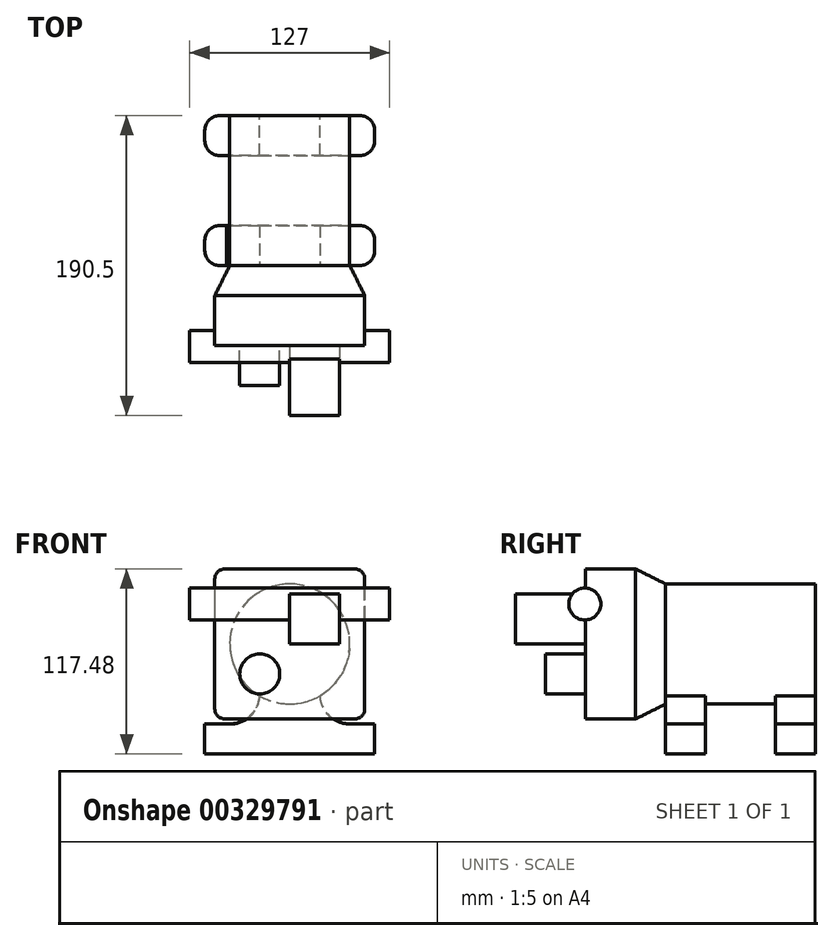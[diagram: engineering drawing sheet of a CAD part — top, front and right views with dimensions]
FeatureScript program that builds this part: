
annotation { "Feature Type Name" : "Feature", "Feature Type Description" : "" }
export const myFeature = defineFeature(function(context is Context, id is Id, definition is map)
    precondition{}
    {
        {
            var Q0;
            Q0=qCreatedBy(makeId("Front.planeOp"),FACE);
            var sketch = newSketch(context, id + "F0", { "sketchPlane" : qUnion([Q0])});
            skCircle(sketch, "E0", {"center": v(0, 0) * mm, "radius": 38.1 * mm});
            skSolve(sketch);
        }
        {
            var Q0;
            Q0 = qSketchRegion(id + "F0", true);
            extrude(context, id + "F1", {"entities" : qUnion([Q0]), "depth" : 95.25 * mm});
        }
        {
            var Q0;
            Q0=makeQuery(id+"F1.opExtrude","CAP_FACE",FACE,{"disambiguationData":[OSD([sQuery(id+"F0.wireOp",EDGE,"E0")])],"isStart":false});
            var sketch = newSketch(context, id + "F2", { "sketchPlane" : qUnion([Q0])});
            skLineSegment(sketch, "E1.bottom", {"start": v(47.63, -47.63) * mm, "end": v(-47.62, -47.63) * mm});
            skLineSegment(sketch, "E1.top", {"start": v(47.62, 47.63) * mm, "end": v(-47.63, 47.62) * mm});
            skLineSegment(sketch, "E1.left", {"start": v(47.63, -47.63) * mm, "end": v(47.62, 47.63) * mm});
            skLineSegment(sketch, "E1.right", {"start": v(-47.62, -47.63) * mm, "end": v(-47.63, 47.62) * mm});
            skPoint(sketch, "E1.middle", {"position": v(0, 0) * mm});
            skPoint(sketch, "E2.visualSharp", {"position": v(47.62, 47.63) * mm});
            skPoint(sketch, "E3.visualSharp", {"position": v(47.63, -47.63) * mm});
            skPoint(sketch, "E4.visualSharp", {"position": v(-47.62, -47.63) * mm});
            skPoint(sketch, "E5.visualSharp", {"position": v(-47.63, 47.62) * mm});
            skSolve(sketch);
        }
        {
            var Q0;
            Q0 = qSketchRegion(id + "F2", true);
            extrude(context, id + "F3", {"entities" : qUnion([Q0]), "depth" : 50.8 * mm, "hasSecondDirection" : true, "secondDirectionOppositeDirection" : false, "secondDirectionDepth" : 19.05 * mm});
        }
        {
            var Q0;
            Q0=makeQuery(id+"F3.opExtrude","SWEPT_EDGE",EDGE,{"disambiguationData":[OSD([sQuery(id+"F2.wireOp",EDGE,"E1.top"),sQuery(id+"F2.wireOp",EDGE,"E1.left")])]});
            var Q1;
            Q1=makeQuery(id+"F3.opExtrude","SWEPT_EDGE",EDGE,{"disambiguationData":[OSD([sQuery(id+"F2.wireOp",EDGE,"E1.bottom"),sQuery(id+"F2.wireOp",EDGE,"E1.left")])]});
            var Q2;
            Q2=makeQuery(id+"F3.opExtrude","SWEPT_EDGE",EDGE,{"disambiguationData":[OSD([sQuery(id+"F2.wireOp",EDGE,"E1.top"),sQuery(id+"F2.wireOp",EDGE,"E1.right")])]});
            var Q3;
            Q3=makeQuery(id+"F3.opExtrude","SWEPT_EDGE",EDGE,{"disambiguationData":[OSD([sQuery(id+"F2.wireOp",EDGE,"E1.bottom"),sQuery(id+"F2.wireOp",EDGE,"E1.right")])]});
            fillet(context, id + "F4", {"entities" : qUnion([Q0, Q1, Q2, Q3]), "radius" : 6.35 * mm, "tangentPropagation" : true, "allowEdgeOverflow" : false});
        }
        {
            var Q1;
            Q1=makeQuery(id+"F3.opExtrude","CAP_FACE",FACE,{"disambiguationData":[OSD([sQuery(id+"F2.wireOp",EDGE,"E1.bottom"),sQuery(id+"F2.wireOp",EDGE,"E1.top"),sQuery(id+"F2.wireOp",EDGE,"E1.left"),sQuery(id+"F2.wireOp",EDGE,"E1.right")])],"isStart":true});
            var Q2;
            Q2=makeQuery(id+"F1.opExtrude","CAP_FACE",FACE,{"disambiguationData":[OSD([sQuery(id+"F0.wireOp",EDGE,"E0")])],"isStart":false});
            loft(context, id + "F5", {"operationType" : NewBodyOperationType.ADD, "sheetProfilesArray" : [{ "sheetProfileEntities" : qUnion([Q1]) }, { "sheetProfileEntities" : qUnion([Q2]) }]});
        }
        {
            var Q0;
            Q0=qCreatedBy(makeId("Right.planeOp"),FACE);
            var sketch = newSketch(context, id + "F6", { "sketchPlane" : qUnion([Q0])});
            skCircle(sketch, "E6", {"center": v(-146.57, 25.4) * mm, "radius": 10.16 * mm});
            skSolve(sketch);
        }
        {
            var Q0;
            {var subQ0=sQuery(id+"F2.wireOp",EDGE,"E1.left");var subQ1=sQuery(id+"F2.wireOp",EDGE,"E1.bottom");var subQ2=sQuery(id+"F2.wireOp",EDGE,"E1.right");Q0=makeQuery(id+"FkyLQc96Iigq7Rs_1.boolean.opBoolean","SPLIT",FACE,{"disambiguationData":[TD([makeQuery(id+"F3.opExtrude","SWEPT_FACE",FACE,{"disambiguationData":[OSD([subQ1])]})])],"derivedFrom":makeQuery(id+"F3.opExtrude","CAP_FACE",FACE,{"disambiguationData":[OSD([subQ1,sQuery(id+"F2.wireOp",EDGE,"E1.top"),subQ0,subQ2])],"isStart":false})});}
            var sketch = newSketch(context, id + "F7", { "sketchPlane" : qUnion([Q0])});
            skLineSegment(sketch, "E7.bottom", {"start": v(0, 0) * mm, "end": v(31.75, 0) * mm});
            skLineSegment(sketch, "E7.top", {"start": v(0, 31.75) * mm, "end": v(31.75, 31.75) * mm});
            skLineSegment(sketch, "E7.left", {"start": v(0, 0) * mm, "end": v(0, 31.75) * mm});
            skLineSegment(sketch, "E7.right", {"start": v(31.75, 0) * mm, "end": v(31.75, 31.75) * mm});
            skCircle(sketch, "E8", {"center": v(-19.05, -19.05) * mm, "radius": 12.7 * mm});
            skSolve(sketch);
        }
        {
            var Q0;
            Q0=makeQuery(id+"F7.imprint","IMPRINT",FACE,{"disambiguationData":[TD([[makeQuery(id+"F7.imprint","IMPRINT",EDGE,{"derivedFrom":sQuery(id+"F7.wireOp",EDGE,"E8")}),1.0]])]});
            extrude(context, id + "F8", {"entities" : qUnion([Q0]), "operationType" : NewBodyOperationType.ADD, "depth" : 25.4 * mm});
        }
        {
            var Q0;
            Q0=makeQuery(id+"F7.imprint","IMPRINT",FACE,{"disambiguationData":[TD([[makeQuery(id+"F7.imprint","IMPRINT",EDGE,{"derivedFrom":sQuery(id+"F7.wireOp",EDGE,"E7.bottom")}),1.0]])]});
            extrude(context, id + "F9", {"entities" : qUnion([Q0]), "operationType" : NewBodyOperationType.ADD, "depth" : 44.45 * mm});
        }
        {
            var Q0;
            Q0 = qSketchRegion(id + "F6", true);
            extrude(context, id + "F10", {"entities" : qUnion([Q0]), "operationType" : NewBodyOperationType.ADD, "depth" : 63.5 * mm, "hasSecondDirection" : true, "secondDirectionOppositeDirection" : true, "secondDirectionDepth" : 63.5 * mm});
        }
        {
            var Q0;
            Q0=qCreatedBy(makeId("Front.planeOp"),FACE);
            var sketch = newSketch(context, id + "F11", { "sketchPlane" : qUnion([Q0])});
            skLineSegment(sketch, "E9.bottom", {"start": v(53.98, -50.8) * mm, "end": v(38.1, -50.8) * mm});
            skLineSegment(sketch, "E9.top", {"start": v(53.98, -69.85) * mm, "end": v(-53.97, -69.85) * mm});
            skLineSegment(sketch, "E9.left", {"start": v(53.98, -50.8) * mm, "end": v(53.98, -69.85) * mm});
            skLineSegment(sketch, "E9.right", {"start": v(-53.98, -50.8) * mm, "end": v(-53.98, -69.85) * mm});
            skArc(sketch, "E10", {"start": v(38.1, -50.8) * mm, "mid": v(25.07, -45.64) * mm, "end": v(19.09, -32.97) * mm});
            skArc(sketch, "E11.MirrorCS", {"start": v(-38.1, -50.8) * mm, "mid": v(-25.07, -45.64) * mm, "end": v(-19.09, -32.97) * mm});
            skLineSegment(sketch, "E12.trimOffspring", {"start": v(-38.1, -50.8) * mm, "end": v(-53.97, -50.8) * mm});
            skLineSegment(sketch, "E13", {"start": v(19.09, -32.97) * mm, "end": v(-19.09, -32.97) * mm});
            skPoint(sketch, "E14.orphan", {"position": v(29.58, -14.71) * mm});
            skPoint(sketch, "E15.orphan", {"position": v(-29.58, -14.71) * mm});
            skSolve(sketch);
        }
        {
            var Q0;
            Q0=qCreatedBy(makeId("Front.planeOp"),FACE);
            cPlane(context, id + "F12", {"entities" : qUnion([Q0]), "cplaneType" : CPlaneType.OFFSET, "offset" : 95.25 * mm, "width" : 152.4 * mm, "height" : 152.4 * mm});
        }
        {
            var Q0;
            Q0=qCreatedBy(id+"F12.planeOp",FACE);
            var sketch = newSketch(context, id + "F13", { "sketchPlane" : qUnion([Q0])});
            skLineSegment(sketch, "E16.bottom", {"start": v(53.97, -50.8) * mm, "end": v(38.1, -50.8) * mm});
            skLineSegment(sketch, "E16.top", {"start": v(53.97, -69.85) * mm, "end": v(-53.98, -69.85) * mm});
            skLineSegment(sketch, "E16.left", {"start": v(53.97, -50.8) * mm, "end": v(53.97, -69.85) * mm});
            skLineSegment(sketch, "E16.right", {"start": v(-53.98, -50.8) * mm, "end": v(-53.98, -69.85) * mm});
            skArc(sketch, "E17", {"start": v(38.1, -50.8) * mm, "mid": v(25.07, -45.64) * mm, "end": v(19.09, -32.97) * mm});
            skArc(sketch, "E18.MirrorCS", {"start": v(-40.26, -50.8) * mm, "mid": v(-25.83, -46.44) * mm, "end": v(-19.09, -32.97) * mm});
            skLineSegment(sketch, "E19.trimOffspring", {"start": v(-40.26, -50.8) * mm, "end": v(-53.98, -50.8) * mm});
            skLineSegment(sketch, "E20", {"start": v(19.09, -32.97) * mm, "end": v(-19.09, -32.97) * mm});
            skSolve(sketch);
        }
        {
            var Q0;
            Q0=makeQuery(id+"F11.imprint","IMPRINT",FACE,{"disambiguationData":[TD([[makeQuery(id+"F11.imprint","IMPRINT",EDGE,{"derivedFrom":sQuery(id+"F11.wireOp",EDGE,"E9.bottom")}),1.0]])]});
            extrude(context, id + "F14", {"entities" : qUnion([Q0]), "operationType" : NewBodyOperationType.ADD, "depth" : 25.4 * mm});
        }
        {
            var Q0;
            Q0 = qSketchRegion(id + "F13", true);
            extrude(context, id + "F15", {"entities" : qUnion([Q0]), "operationType" : NewBodyOperationType.ADD, "oppositeDirection" : true, "depth" : 25.4 * mm});
        }
        {
            var Q0;
            Q0=makeQuery(id+"F14.opExtrude","CAP_EDGE",EDGE,{"disambiguationData":[OSD([sQuery(id+"F11.wireOp",EDGE,"E9.right")])],"isStart":true});
            var Q1;
            Q1=makeQuery(id+"F14.opExtrude","CAP_EDGE",EDGE,{"disambiguationData":[OSD([sQuery(id+"F11.wireOp",EDGE,"E9.right")])],"isStart":false});
            var Q2;
            Q2=makeQuery(id+"F14.opExtrude","CAP_EDGE",EDGE,{"disambiguationData":[OSD([sQuery(id+"F11.wireOp",EDGE,"E9.left")])],"isStart":true});
            var Q3;
            Q3=makeQuery(id+"F15.opExtrude","CAP_EDGE",EDGE,{"disambiguationData":[OSD([sQuery(id+"F13.wireOp",EDGE,"E16.right")])],"isStart":false});
            var Q4;
            Q4=makeQuery(id+"F15.opExtrude","CAP_EDGE",EDGE,{"disambiguationData":[OSD([sQuery(id+"F13.wireOp",EDGE,"E16.right")])],"isStart":true});
            var Q5;
            Q5=makeQuery(id+"F14.opExtrude","CAP_EDGE",EDGE,{"disambiguationData":[OSD([sQuery(id+"F11.wireOp",EDGE,"E9.left")])],"isStart":false});
            var Q6;
            Q6=makeQuery(id+"F15.opExtrude","CAP_EDGE",EDGE,{"disambiguationData":[OSD([sQuery(id+"F13.wireOp",EDGE,"E16.left")])],"isStart":false});
            var Q7;
            Q7=makeQuery(id+"F15.opExtrude","CAP_EDGE",EDGE,{"disambiguationData":[OSD([sQuery(id+"F13.wireOp",EDGE,"E16.left")])],"isStart":true});
            fillet(context, id + "F16", {"entities" : qUnion([Q0, Q1, Q2, Q3, Q4, Q5, Q6, Q7]), "radius" : 9.52 * mm, "tangentPropagation" : true, "allowEdgeOverflow" : false});
        }
    });
